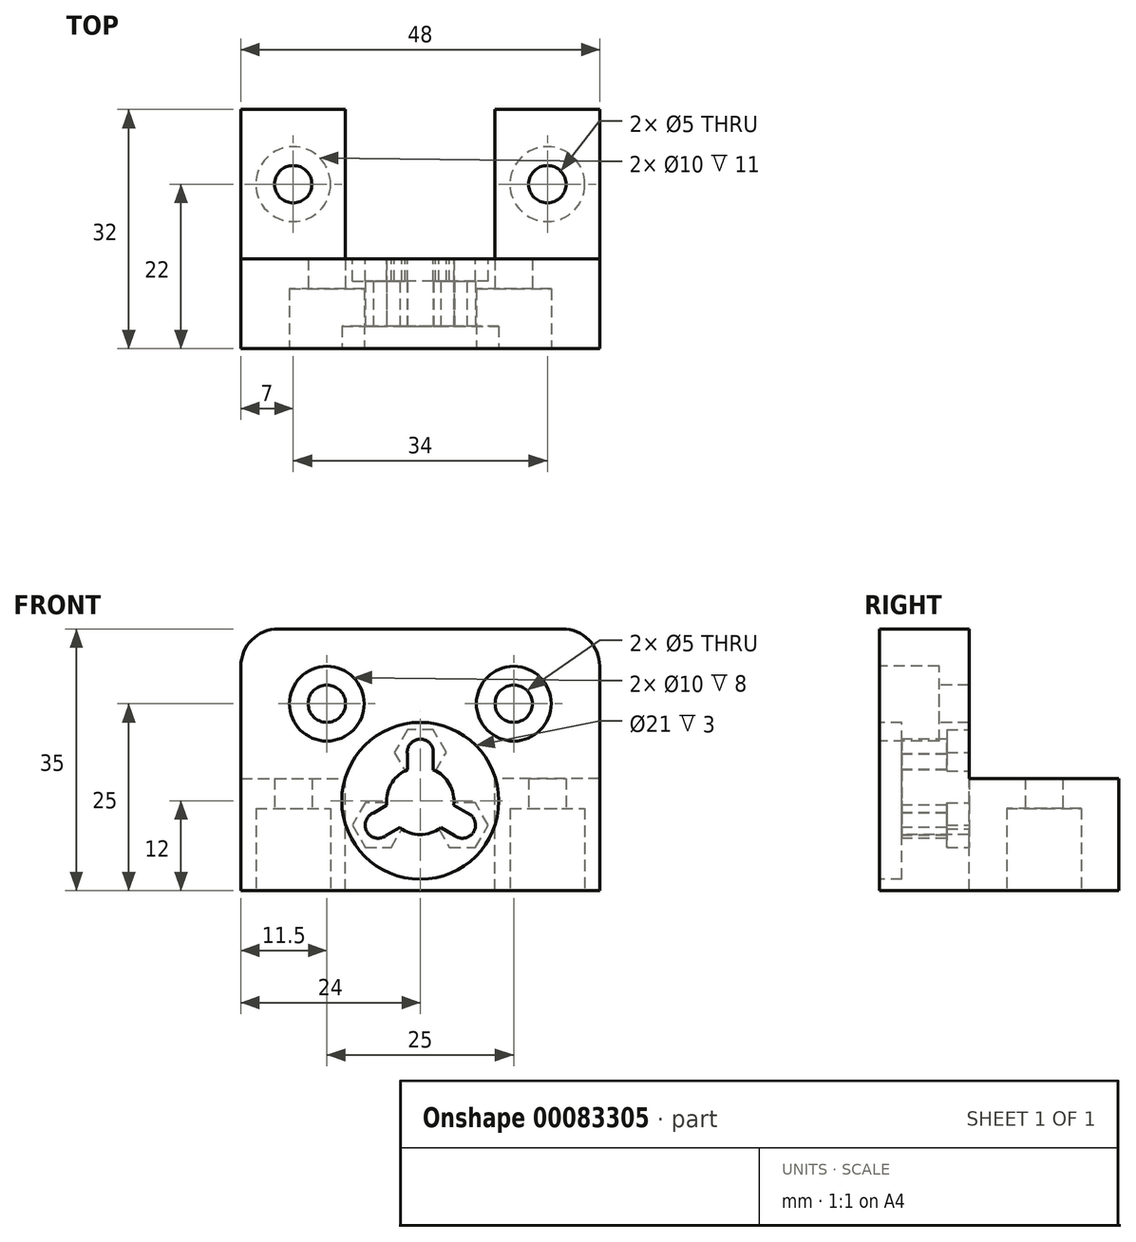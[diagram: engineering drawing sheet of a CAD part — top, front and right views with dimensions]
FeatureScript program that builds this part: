
annotation { "Feature Type Name" : "Feature", "Feature Type Description" : "" }
export const myFeature = defineFeature(function(context is Context, id is Id, definition is map)
    precondition{}
    {
        {
            var Q0;
            Q0=qCreatedBy(makeId("Front.planeOp"),FACE);
            var sketch = newSketch(context, id + "F0", { "sketchPlane" : qUnion([Q0])});
            skLineSegment(sketch, "E0.bottom", {"start": v(-24, -12) * mm, "end": v(24, -12) * mm});
            skLineSegment(sketch, "E0.top", {"start": v(-24, 23) * mm, "end": v(24, 23) * mm});
            skLineSegment(sketch, "E0.left", {"start": v(-24, -12) * mm, "end": v(-24, 23) * mm});
            skLineSegment(sketch, "E0.right", {"start": v(24, -12) * mm, "end": v(24, 23) * mm});
            skArc(sketch, "E1", {"start": v(-2.74, -3.57) * mm, "mid": v(0, -4.5) * mm, "end": v(2.73, -3.58) * mm});
            skCircle(sketch, "E2.cCircle", {"center": v(0, 0) * mm, "radius": 6.5 * mm, "construction": true});
            skLineSegment(sketch, "E2.0", {"start": v(0, 6.5) * mm, "end": v(5.63, -3.25) * mm, "construction": true});
            skLineSegment(sketch, "E2.1", {"start": v(5.63, -3.25) * mm, "end": v(-5.63, -3.25) * mm, "construction": true});
            skLineSegment(sketch, "E2.2", {"start": v(-5.63, -3.25) * mm, "end": v(0, 6.5) * mm, "construction": true});
            skCircle(sketch, "E3", {"center": v(0, 0) * mm, "radius": 10.5 * mm});
            skCircle(sketch, "E4", {"center": v(0, 6.5) * mm, "radius": 1.75 * mm});
            skCircle(sketch, "E5", {"center": v(5.63, -3.25) * mm, "radius": 1.75 * mm});
            skCircle(sketch, "E6", {"center": v(-5.63, -3.25) * mm, "radius": 1.75 * mm});
            skLineSegment(sketch, "E7", {"start": v(0, -14.58) * mm, "end": v(0, 17.23) * mm, "construction": true});
            skLineSegment(sketch, "E8", {"start": v(-16.58, 0) * mm, "end": v(25.82, 0) * mm, "construction": true});
            skCircle(sketch, "E9", {"center": v(-12.5, 13) * mm, "radius": 2.5 * mm});
            skCircle(sketch, "E10", {"center": v(12.5, 13) * mm, "radius": 2.5 * mm});
            skCircle(sketch, "E11", {"center": v(-12.5, 13) * mm, "radius": 5 * mm});
            skCircle(sketch, "E12", {"center": v(12.5, 13) * mm, "radius": 5 * mm});
            skLineSegment(sketch, "E13", {"start": v(-4.5, 0) * mm, "end": v(-4.5, -4.59) * mm});
            skLineSegment(sketch, "E14", {"start": v(0, 0) * mm, "end": v(-5.63, -3.25) * mm, "construction": true});
            skLineSegment(sketch, "E15", {"start": v(0, 0) * mm, "end": v(0, 6.5) * mm, "construction": true});
            skLineSegment(sketch, "E16", {"start": v(0, 0) * mm, "end": v(5.63, -3.25) * mm, "construction": true});
            skLineSegment(sketch, "E17", {"start": v(-2.74, -3.57) * mm, "end": v(-4.5, -4.59) * mm});
            skLineSegment(sketch, "E18", {"start": v(-6.3, -1.63) * mm, "end": v(-4.46, -0.57) * mm});
            skLineSegment(sketch, "E19.1.0", {"start": v(4.56, -4.63) * mm, "end": v(2.73, -3.58) * mm});
            skLineSegment(sketch, "E19.1.1", {"start": v(4.46, -0.59) * mm, "end": v(6.22, -1.6) * mm});
            skLineSegment(sketch, "E19.2.0", {"start": v(1.73, 6.26) * mm, "end": v(1.73, 4.15) * mm});
            skLineSegment(sketch, "E19.2.1", {"start": v(-1.72, 4.16) * mm, "end": v(-1.72, 6.2) * mm});
            skArc(sketch, "E20.trimOffspring", {"start": v(-1.72, 4.16) * mm, "mid": v(-3.9, 2.26) * mm, "end": v(-4.46, -0.57) * mm});
            skArc(sketch, "E21.trimOffspring", {"start": v(4.46, -0.59) * mm, "mid": v(3.9, 2.24) * mm, "end": v(1.73, 4.15) * mm});
            skSolve(sketch);
        }
        {
            var Q0;
            Q0=makeQuery(id+"F0.imprint","IMPRINT",FACE,{"disambiguationData":[TD([[makeQuery(id+"F0.imprint","IMPRINT",EDGE,{"derivedFrom":sQuery(id+"F0.wireOp",EDGE,"E0.bottom")}),1.0]])]});
            var Q1;
            Q1=makeQuery(id+"F0.imprint","IMPRINT",FACE,{"disambiguationData":[TD([[makeQuery(id+"F0.imprint","IMPRINT",EDGE,{"derivedFrom":sQuery(id+"F0.wireOp",EDGE,"E9")}),-1.0]])]});
            var Q2;
            Q2=makeQuery(id+"F0.imprint","IMPRINT",FACE,{"disambiguationData":[TD([[makeQuery(id+"F0.imprint","IMPRINT",EDGE,{"derivedFrom":sQuery(id+"F0.wireOp",EDGE,"E10")}),-1.0]])]});
            var Q3;
            Q3=makeQuery(id+"F0.imprint","IMPRINT",FACE,{"disambiguationData":[TD([[makeQuery(id+"F0.imprint","IMPRINT",EDGE,{"derivedFrom":sQuery(id+"F0.wireOp",EDGE,"E1")}),-1.0]])]});
            extrude(context, id + "F1", {"entities" : qUnion([Q0, Q1, Q2, Q3]), "oppositeDirection" : true, "depth" : 12 * mm});
        }
        {
            var Q0;
            Q0=makeQuery(id+"F0.imprint","IMPRINT",FACE,{"disambiguationData":[TD([[makeQuery(id+"F0.imprint","IMPRINT",EDGE,{"derivedFrom":sQuery(id+"F0.wireOp",EDGE,"E10")}),-1.0]])]});
            var Q1;
            Q1=makeQuery(id+"F0.imprint","IMPRINT",FACE,{"disambiguationData":[TD([[makeQuery(id+"F0.imprint","IMPRINT",EDGE,{"derivedFrom":sQuery(id+"F0.wireOp",EDGE,"E9")}),-1.0]])]});
            extrude(context, id + "F2", {"entities" : qUnion([Q0, Q1]), "operationType" : NewBodyOperationType.REMOVE, "oppositeDirection" : true, "depth" : 8 * mm});
        }
        {
            var Q0;
            Q0=makeQuery(id+"F0.imprint","IMPRINT",FACE,{"disambiguationData":[TD([[makeQuery(id+"F0.imprint","IMPRINT",EDGE,{"derivedFrom":sQuery(id+"F0.wireOp",EDGE,"E1")}),-1.0]])]});
            extrude(context, id + "F3", {"entities" : qUnion([Q0]), "operationType" : NewBodyOperationType.REMOVE, "oppositeDirection" : true, "depth" : 3 * mm});
        }
        {
            var Q0;
            Q0=makeQuery(id+"F1.opExtrude","CAP_FACE",FACE,{"disambiguationData":[OSD([sQuery(id+"F0.wireOp",EDGE,"E0.bottom"),sQuery(id+"F0.wireOp",EDGE,"E0.top"),sQuery(id+"F0.wireOp",EDGE,"E0.left"),sQuery(id+"F0.wireOp",EDGE,"E0.right"),sQuery(id+"F0.wireOp",EDGE,"E1"),sQuery(id+"F0.wireOp",EDGE,"E4"),sQuery(id+"F0.wireOp",EDGE,"E5"),sQuery(id+"F0.wireOp",EDGE,"E6"),sQuery(id+"F0.wireOp",EDGE,"E9"),sQuery(id+"F0.wireOp",EDGE,"E10")])],"isStart":false});
            var sketch = newSketch(context, id + "F4", { "sketchPlane" : qUnion([Q0])});
            skCircle(sketch, "E22", {"center": v(0, 0) * mm, "radius": 3.5 * mm, "construction": true});
            skCircle(sketch, "E23.cCircle", {"center": v(0, 6.5) * mm, "radius": 3 * mm, "construction": true});
            skLineSegment(sketch, "E23.0", {"start": v(-1.73, 9.5) * mm, "end": v(1.73, 9.5) * mm});
            skLineSegment(sketch, "E23.1", {"start": v(1.73, 9.5) * mm, "end": v(3.46, 6.5) * mm});
            skLineSegment(sketch, "E23.2", {"start": v(3.46, 6.5) * mm, "end": v(1.73, 3.5) * mm});
            skLineSegment(sketch, "E23.3", {"start": v(1.73, 3.5) * mm, "end": v(-1.73, 3.5) * mm, "construction": true});
            skLineSegment(sketch, "E23.4", {"start": v(-1.73, 3.5) * mm, "end": v(-3.46, 6.5) * mm});
            skLineSegment(sketch, "E23.5", {"start": v(-3.46, 6.5) * mm, "end": v(-1.73, 9.5) * mm});
            skPoint(sketch, "E23.0.midPoint", {"position": v(0, 9.5) * mm});
            skPoint(sketch, "E24.1.1", {"position": v(-8.23, -4.75) * mm});
            skCircle(sketch, "E24.1.2", {"center": v(-5.63, -3.25) * mm, "radius": 3 * mm, "construction": true});
            skLineSegment(sketch, "E24.1.3", {"start": v(-7.36, -0.25) * mm, "end": v(-3.9, -0.25) * mm});
            skLineSegment(sketch, "E24.1.4", {"start": v(-7.36, -6.25) * mm, "end": v(-9.1, -3.25) * mm});
            skLineSegment(sketch, "E24.1.5", {"start": v(-3.9, -0.25) * mm, "end": v(-2.17, -3.25) * mm, "construction": true});
            skLineSegment(sketch, "E24.1.6", {"start": v(-2.17, -3.25) * mm, "end": v(-3.9, -6.25) * mm});
            skLineSegment(sketch, "E24.1.7", {"start": v(-3.9, -6.25) * mm, "end": v(-7.36, -6.25) * mm});
            skLineSegment(sketch, "E24.1.8", {"start": v(-9.1, -3.25) * mm, "end": v(-7.36, -0.25) * mm});
            skCircle(sketch, "E24.2.0", {"center": v(0, 0) * mm, "radius": 3.5 * mm});
            skPoint(sketch, "E24.2.1", {"position": v(8.23, -4.75) * mm});
            skCircle(sketch, "E24.2.2", {"center": v(5.63, -3.25) * mm, "radius": 3 * mm, "construction": true});
            skLineSegment(sketch, "E24.2.3", {"start": v(3.9, -6.25) * mm, "end": v(2.17, -3.25) * mm});
            skLineSegment(sketch, "E24.2.4", {"start": v(9.1, -3.25) * mm, "end": v(7.36, -6.25) * mm});
            skLineSegment(sketch, "E24.2.5", {"start": v(2.17, -3.25) * mm, "end": v(3.9, -0.25) * mm, "construction": true});
            skLineSegment(sketch, "E24.2.6", {"start": v(3.9, -0.25) * mm, "end": v(7.36, -0.25) * mm});
            skLineSegment(sketch, "E24.2.7", {"start": v(7.36, -0.25) * mm, "end": v(9.1, -3.25) * mm});
            skLineSegment(sketch, "E24.2.8", {"start": v(7.36, -6.25) * mm, "end": v(3.9, -6.25) * mm});
            skLineSegment(sketch, "E25", {"start": v(-1.73, 3.5) * mm, "end": v(-3.9, -0.25) * mm});
            skLineSegment(sketch, "E26", {"start": v(1.73, 3.5) * mm, "end": v(3.9, -0.25) * mm});
            skLineSegment(sketch, "E27", {"start": v(2.17, -3.25) * mm, "end": v(-2.17, -3.25) * mm});
            skLineSegment(sketch, "E28.bottom", {"start": v(-24, -12) * mm, "end": v(-10, -12) * mm});
            skLineSegment(sketch, "E28.top", {"start": v(-24, 3) * mm, "end": v(-10, 3) * mm});
            skLineSegment(sketch, "E28.left", {"start": v(-24, -12) * mm, "end": v(-24, 3) * mm});
            skLineSegment(sketch, "E28.right", {"start": v(-10, -12) * mm, "end": v(-10, 3) * mm});
            skLineSegment(sketch, "E29.bottom", {"start": v(24, -12) * mm, "end": v(10, -12) * mm});
            skLineSegment(sketch, "E29.top", {"start": v(24, 3) * mm, "end": v(10, 3) * mm});
            skLineSegment(sketch, "E29.left", {"start": v(24, -12) * mm, "end": v(24, 3) * mm});
            skLineSegment(sketch, "E29.right", {"start": v(10, -12) * mm, "end": v(10, 3) * mm});
            skSolve(sketch);
        }
        {
            var Q0;
            Q0=makeQuery(id+"F4.imprint","IMPRINT",FACE,{"disambiguationData":[TD([[makeQuery(id+"F4.imprint","IMPRINT",EDGE,{"derivedFrom":sQuery(id+"F4.wireOp",EDGE,"E24.1.4")}),-1.0]])]});
            var Q1;
            Q1=makeQuery(id+"F4.imprint","IMPRINT",FACE,{"disambiguationData":[TD([[makeQuery(id+"F4.imprint","IMPRINT",EDGE,{"derivedFrom":sQuery(id+"F4.wireOp",EDGE,"E23.0")}),-1.0]])]});
            var Q2;
            Q2=makeQuery(id+"F4.imprint","IMPRINT",FACE,{"disambiguationData":[TD([[makeQuery(id+"F4.imprint","IMPRINT",EDGE,{"derivedFrom":sQuery(id+"F4.wireOp",EDGE,"E24.2.4")}),-1.0]])]});
            extrude(context, id + "F5", {"entities" : qUnion([Q0, Q1, Q2]), "operationType" : NewBodyOperationType.REMOVE, "oppositeDirection" : true, "depth" : 3 * mm});
        }
        {
            var Q0;
            Q0=makeQuery(id+"F4.imprint","IMPRINT",FACE,{"disambiguationData":[TD([[makeQuery(id+"F4.imprint","IMPRINT",EDGE,{"derivedFrom":sQuery(id+"F4.wireOp",EDGE,"E28.bottom")}),-1.0]])]});
            var Q1;
            Q1=makeQuery(id+"F4.imprint","IMPRINT",FACE,{"disambiguationData":[TD([[makeQuery(id+"F4.imprint","IMPRINT",EDGE,{"derivedFrom":sQuery(id+"F4.wireOp",EDGE,"E29.bottom")}),-1.0]])]});
            extrude(context, id + "F6", {"entities" : qUnion([Q0, Q1]), "operationType" : NewBodyOperationType.ADD, "depth" : 20 * mm});
        }
        {
            var Q0;
            Q0=makeQuery(id+"F6.boolean.opBoolean","MERGE",FACE,{"derivedFrom":[makeQuery(id+"F1.opExtrude","SWEPT_FACE",FACE,{"disambiguationData":[OSD([sQuery(id+"F0.wireOp",EDGE,"E0.bottom")])]}),makeQuery(id+"F6.opExtrude","SWEPT_FACE",FACE,{"disambiguationData":[OSD([sQuery(id+"F4.wireOp",EDGE,"E28.bottom")])]}),makeQuery(id+"F6.opExtrude","SWEPT_FACE",FACE,{"disambiguationData":[OSD([sQuery(id+"F4.wireOp",EDGE,"E29.bottom")])]})]});
            var sketch = newSketch(context, id + "F7", { "sketchPlane" : qUnion([Q0])});
            skCircle(sketch, "E30", {"center": v(-17, -22) * mm, "radius": 2.5 * mm});
            skCircle(sketch, "E31", {"center": v(17, -22) * mm, "radius": 2.5 * mm});
            skCircle(sketch, "E32", {"center": v(-17, -22) * mm, "radius": 5 * mm});
            skCircle(sketch, "E33", {"center": v(17, -22) * mm, "radius": 5 * mm});
            skSolve(sketch);
        }
        {
            var Q0;
            Q0=makeQuery(id+"F7.imprint","IMPRINT",FACE,{"disambiguationData":[TD([[makeQuery(id+"F7.imprint","IMPRINT",EDGE,{"derivedFrom":sQuery(id+"F7.wireOp",EDGE,"E30")}),1.0]])]});
            var Q1;
            Q1=makeQuery(id+"F7.imprint","IMPRINT",FACE,{"disambiguationData":[TD([[makeQuery(id+"F7.imprint","IMPRINT",EDGE,{"derivedFrom":sQuery(id+"F7.wireOp",EDGE,"E31")}),1.0]])]});
            extrude(context, id + "F8", {"entities" : qUnion([Q0, Q1]), "operationType" : NewBodyOperationType.REMOVE, "endBound" : BoundingType.THROUGH_ALL, "oppositeDirection" : true, "depth" : 25 * mm});
        }
        {
            var Q0;
            Q0=makeQuery(id+"F1.opExtrude","SWEPT_EDGE",EDGE,{"disambiguationData":[OSD([sQuery(id+"F0.wireOp",EDGE,"E0.top"),sQuery(id+"F0.wireOp",EDGE,"E0.left")])]});
            var Q1;
            Q1=makeQuery(id+"F1.opExtrude","SWEPT_EDGE",EDGE,{"disambiguationData":[OSD([sQuery(id+"F0.wireOp",EDGE,"E0.top"),sQuery(id+"F0.wireOp",EDGE,"E0.right")])]});
            fillet(context, id + "F9", {"entities" : qUnion([Q0, Q1]), "radius" : 5 * mm, "tangentPropagation" : true, "allowEdgeOverflow" : false});
        }
        {
            var Q0;
            Q0=makeQuery(id+"F7.imprint","IMPRINT",FACE,{"disambiguationData":[TD([[makeQuery(id+"F7.imprint","IMPRINT",EDGE,{"derivedFrom":sQuery(id+"F7.wireOp",EDGE,"E30")}),-1.0]])]});
            var Q1;
            Q1=makeQuery(id+"F7.imprint","IMPRINT",FACE,{"disambiguationData":[TD([[makeQuery(id+"F7.imprint","IMPRINT",EDGE,{"derivedFrom":sQuery(id+"F7.wireOp",EDGE,"E31")}),-1.0]])]});
            extrude(context, id + "F10", {"entities" : qUnion([Q0, Q1]), "operationType" : NewBodyOperationType.REMOVE, "oppositeDirection" : true, "depth" : 11 * mm});
        }
    });
